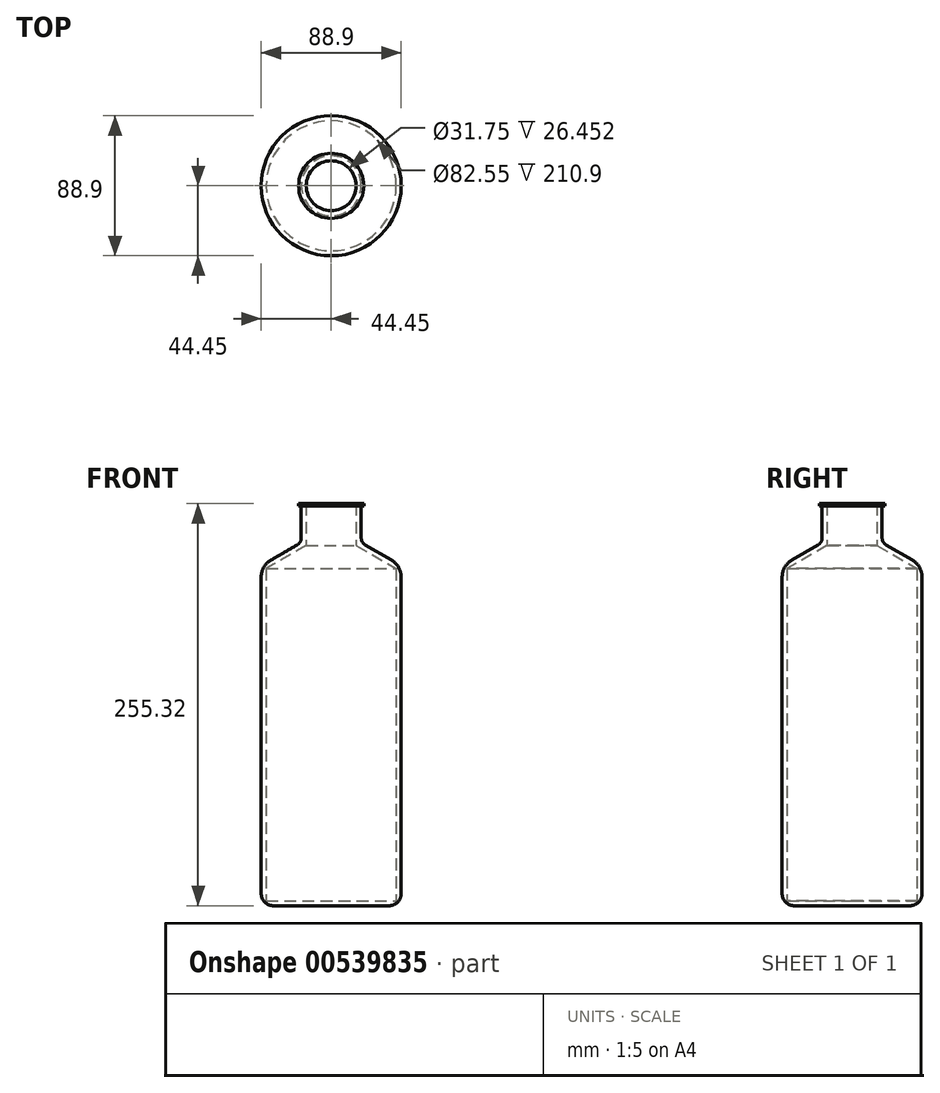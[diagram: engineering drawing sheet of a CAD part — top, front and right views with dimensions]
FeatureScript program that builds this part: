
annotation { "Feature Type Name" : "Feature", "Feature Type Description" : "" }
export const myFeature = defineFeature(function(context is Context, id is Id, definition is map)
    precondition{}
    {
        {
            var Q0;
            Q0=qCreatedBy(makeId("Front.planeOp"),FACE);
            var sketch = newSketch(context, id + "F0", { "sketchPlane" : qUnion([Q0])});
            skLineSegment(sketch, "E0", {"start": v(0, -66.26) * mm, "end": v(44.45, -66.26) * mm});
            skLineSegment(sketch, "E1", {"start": v(44.45, -66.26) * mm, "end": v(44.45, 149.64) * mm});
            skLineSegment(sketch, "E2", {"start": v(44.45, 149.64) * mm, "end": v(19.05, 164.43) * mm});
            skLineSegment(sketch, "E3", {"start": v(19.05, 164.43) * mm, "end": v(19.05, 187.74) * mm});
            skLineSegment(sketch, "E4", {"start": v(0, -66.26) * mm, "end": v(0, -63.08) * mm});
            skLineSegment(sketch, "E5", {"start": v(0, -63.08) * mm, "end": v(41.28, -63.08) * mm});
            skLineSegment(sketch, "E6", {"start": v(41.28, -63.08) * mm, "end": v(41.28, 147.82) * mm});
            skLineSegment(sketch, "E7", {"start": v(41.28, 147.82) * mm, "end": v(15.88, 162.6) * mm});
            skLineSegment(sketch, "E8", {"start": v(15.88, 162.6) * mm, "end": v(15.88, 189.06) * mm});
            skLineSegment(sketch, "E9", {"start": v(19.05, 187.74) * mm, "end": v(20.7, 187.74) * mm});
            skLineSegment(sketch, "E10", {"start": v(20.7, 187.74) * mm, "end": v(20.7, 189.06) * mm});
            skLineSegment(sketch, "E11", {"start": v(20.7, 189.06) * mm, "end": v(15.88, 189.06) * mm});
            skSolve(sketch);
        }
        {
            var Q0;
            Q0=qCreatedBy(makeId("Front.planeOp"),FACE);
            var sketch = newSketch(context, id + "F1", { "sketchPlane" : qUnion([Q0])});
            skLineSegment(sketch, "E12", {"start": v(0, -74.5) * mm, "end": v(0, 198.91) * mm, "construction": true});
            skSolve(sketch);
        }
        {
            var Q0;
            Q0 = qSketchRegion(id + "F0", true);
            var Q1;
            Q1=sQuery(id+"F1.wireOp",EDGE,"E12");
            revolve(context, id + "F2", {"entities" : qUnion([Q0]), "axis" : qUnion([Q1]), "revolveType" : RevolveType.FULL});
        }
        {
            var Q0;
            Q0=makeQuery(id+"F2.opRevolve","SWEPT_EDGE",EDGE,{"disambiguationData":[OSD([sQuery(id+"F0.wireOp",EDGE,"E0"),sQuery(id+"F0.wireOp",EDGE,"E1")])]});
            fillet(context, id + "F3", {"entities" : qUnion([Q0]), "radius" : 7.62 * mm, "tangentPropagation" : true, "allowEdgeOverflow" : false});
        }
        {
            var Q0;
            Q0=makeQuery(id+"F2.opRevolve","SWEPT_EDGE",EDGE,{"disambiguationData":[OSD([sQuery(id+"F0.wireOp",EDGE,"E1"),sQuery(id+"F0.wireOp",EDGE,"E2")])]});
            fillet(context, id + "F4", {"entities" : qUnion([Q0]), "radius" : 12.7 * mm, "tangentPropagation" : true, "allowEdgeOverflow" : false});
        }
        {
            var Q0;
            Q0=makeQuery(id+"F2.opRevolve","SWEPT_EDGE",EDGE,{"disambiguationData":[OSD([sQuery(id+"F0.wireOp",EDGE,"E2"),sQuery(id+"F0.wireOp",EDGE,"E3")])]});
            fillet(context, id + "F5", {"entities" : qUnion([Q0]), "radius" : 5.08 * mm, "tangentPropagation" : true, "allowEdgeOverflow" : false});
        }
    });
